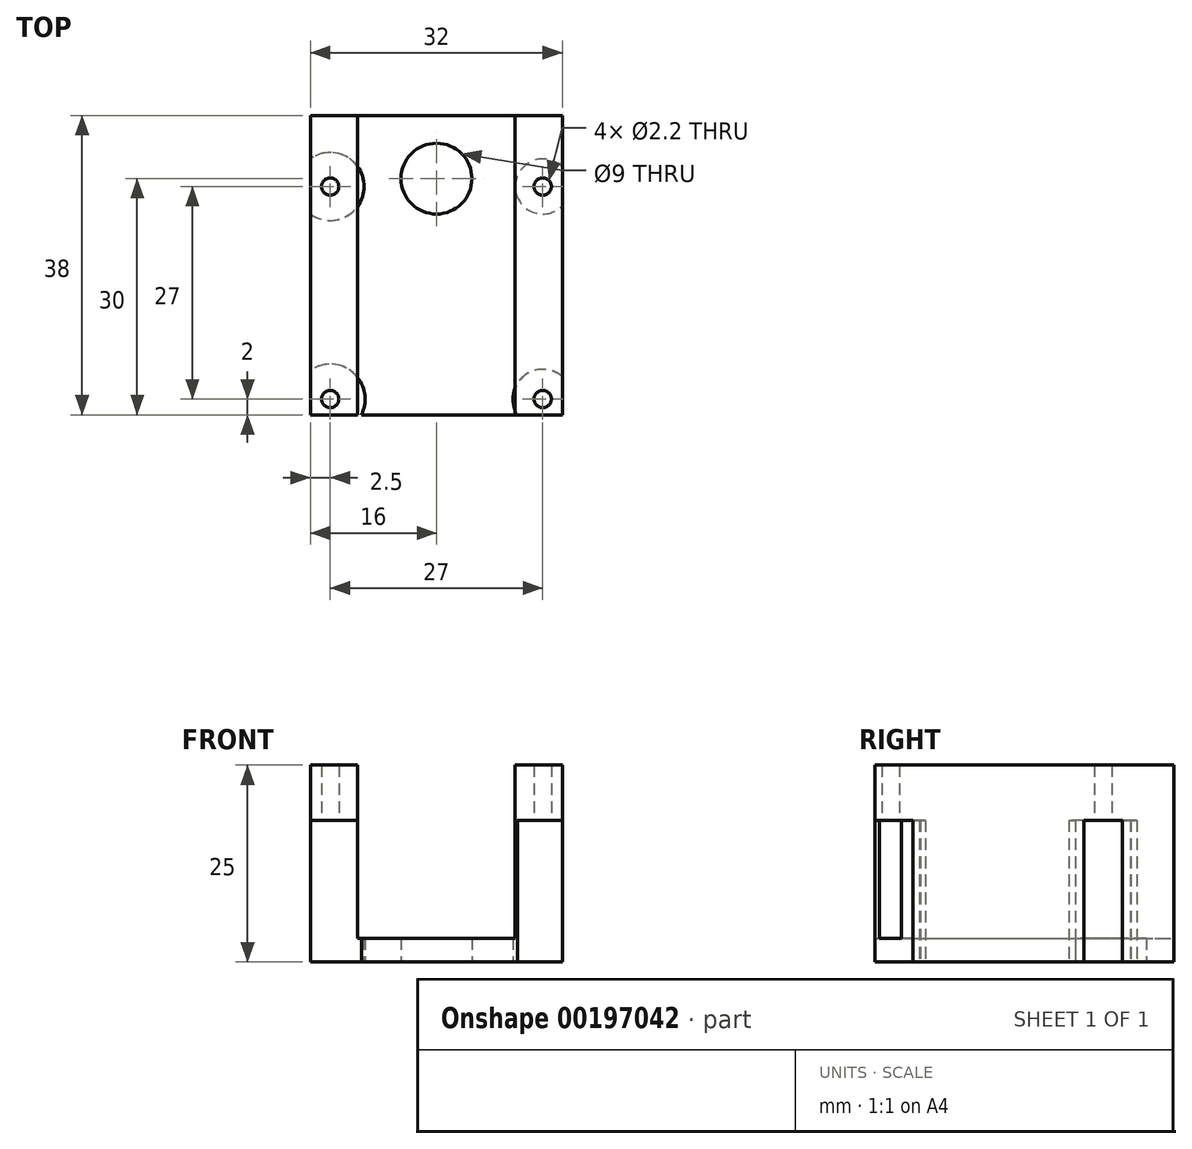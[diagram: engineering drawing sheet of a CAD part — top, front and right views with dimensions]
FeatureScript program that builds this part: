
annotation { "Feature Type Name" : "Feature", "Feature Type Description" : "" }
export const myFeature = defineFeature(function(context is Context, id is Id, definition is map)
    precondition{}
    {
        {
            var Q0;
            Q0=qCreatedBy(makeId("Top.planeOp"),FACE);
            var sketch = newSketch(context, id + "F0", { "sketchPlane" : qUnion([Q0])});
            skCircle(sketch, "E0", {"center": v(0, 0) * mm, "radius": 4.5 * mm});
            skCircle(sketch, "E1", {"center": v(-13.5, -1) * mm, "radius": 1.1 * mm});
            skCircle(sketch, "E2", {"center": v(13.5, -1) * mm, "radius": 1.1 * mm});
            skCircle(sketch, "E3", {"center": v(13.5, -28) * mm, "radius": 1.1 * mm});
            skCircle(sketch, "E4", {"center": v(-13.5, -28) * mm, "radius": 1.1 * mm});
            skLineSegment(sketch, "E5.bottom", {"start": v(-16, 8) * mm, "end": v(16, 8) * mm});
            skLineSegment(sketch, "E5.top", {"start": v(-16, -30) * mm, "end": v(16, -30) * mm});
            skLineSegment(sketch, "E5.left", {"start": v(-16, 8) * mm, "end": v(-16, -30) * mm});
            skLineSegment(sketch, "E5.right", {"start": v(16, 8) * mm, "end": v(16, -30) * mm});
            skSolve(sketch);
        }
        {
            var Q0;
            Q0 = qSketchRegion(id + "F0", true);
            extrude(context, id + "F1", {"entities" : qUnion([Q0]), "depth" : 25 * mm});
        }
        {
            var Q0;
            Q0=makeQuery(id+"F1.opExtrude","SWEPT_FACE",FACE,{"disambiguationData":[OSD([sQuery(id+"F0.wireOp",EDGE,"E5.bottom")])]});
            var sketch = newSketch(context, id + "F2", { "sketchPlane" : qUnion([Q0])});
            skLineSegment(sketch, "E6.bottom", {"start": v(-10, 25) * mm, "end": v(10, 25) * mm});
            skLineSegment(sketch, "E6.top", {"start": v(-10, 3) * mm, "end": v(10, 3) * mm});
            skLineSegment(sketch, "E6.left", {"start": v(-10, 25) * mm, "end": v(-10, 3) * mm});
            skLineSegment(sketch, "E6.right", {"start": v(10, 25) * mm, "end": v(10, 3) * mm});
            skSolve(sketch);
        }
        {
            var Q0;
            Q0 = qSketchRegion(id + "F2", true);
            extrude(context, id + "F3", {"entities" : qUnion([Q0]), "operationType" : NewBodyOperationType.REMOVE, "endBound" : BoundingType.THROUGH_ALL, "oppositeDirection" : true, "depth" : 25 * mm});
        }
        {
            var Q0;
            Q0=makeQuery(id+"F1.opExtrude","CAP_FACE",FACE,{"disambiguationData":[OSD([sQuery(id+"F0.wireOp",EDGE,"E0"),sQuery(id+"F0.wireOp",EDGE,"E1"),sQuery(id+"F0.wireOp",EDGE,"E2"),sQuery(id+"F0.wireOp",EDGE,"E3"),sQuery(id+"F0.wireOp",EDGE,"E4"),sQuery(id+"F0.wireOp",EDGE,"E5.bottom"),sQuery(id+"F0.wireOp",EDGE,"E5.top"),sQuery(id+"F0.wireOp",EDGE,"E5.left"),sQuery(id+"F0.wireOp",EDGE,"E5.right")])],"isStart":true});
            var sketch = newSketch(context, id + "F4", { "sketchPlane" : qUnion([Q0])});
            skArc(sketch, "E7", {"start": v(16, 3.44) * mm, "mid": v(10, 1) * mm, "end": v(16, -1.44) * mm});
            skArc(sketch, "E8", {"start": v(-16, 4.52) * mm, "mid": v(-9.18, 1) * mm, "end": v(-16, -2.52) * mm});
            skArc(sketch, "E9", {"start": v(16, 25.18) * mm, "mid": v(11.06, 25.12) * mm, "end": v(10.3, 30) * mm});
            skArc(sketch, "E10", {"start": v(-16, 24.34) * mm, "mid": v(-10.58, 24.67) * mm, "end": v(-9.55, 30) * mm});
            skLineSegment(sketch, "E11", {"start": v(16, -1.44) * mm, "end": v(16, 3.44) * mm});
            skLineSegment(sketch, "E12", {"start": v(-16, -2.52) * mm, "end": v(-16, 4.52) * mm});
            skLineSegment(sketch, "E13", {"start": v(16, 25.18) * mm, "end": v(16, 30) * mm});
            skLineSegment(sketch, "E14", {"start": v(16, 30) * mm, "end": v(10.3, 30) * mm});
            skLineSegment(sketch, "E15", {"start": v(-9.55, 30) * mm, "end": v(-16, 30) * mm});
            skLineSegment(sketch, "E16", {"start": v(-16, 30) * mm, "end": v(-16, 24.34) * mm});
            skSolve(sketch);
        }
        {
            var Q0;
            Q0 = qSketchRegion(id + "F4", true);
            extrude(context, id + "F5", {"entities" : qUnion([Q0]), "operationType" : NewBodyOperationType.REMOVE, "oppositeDirection" : true, "depth" : 18 * mm});
        }
    });
